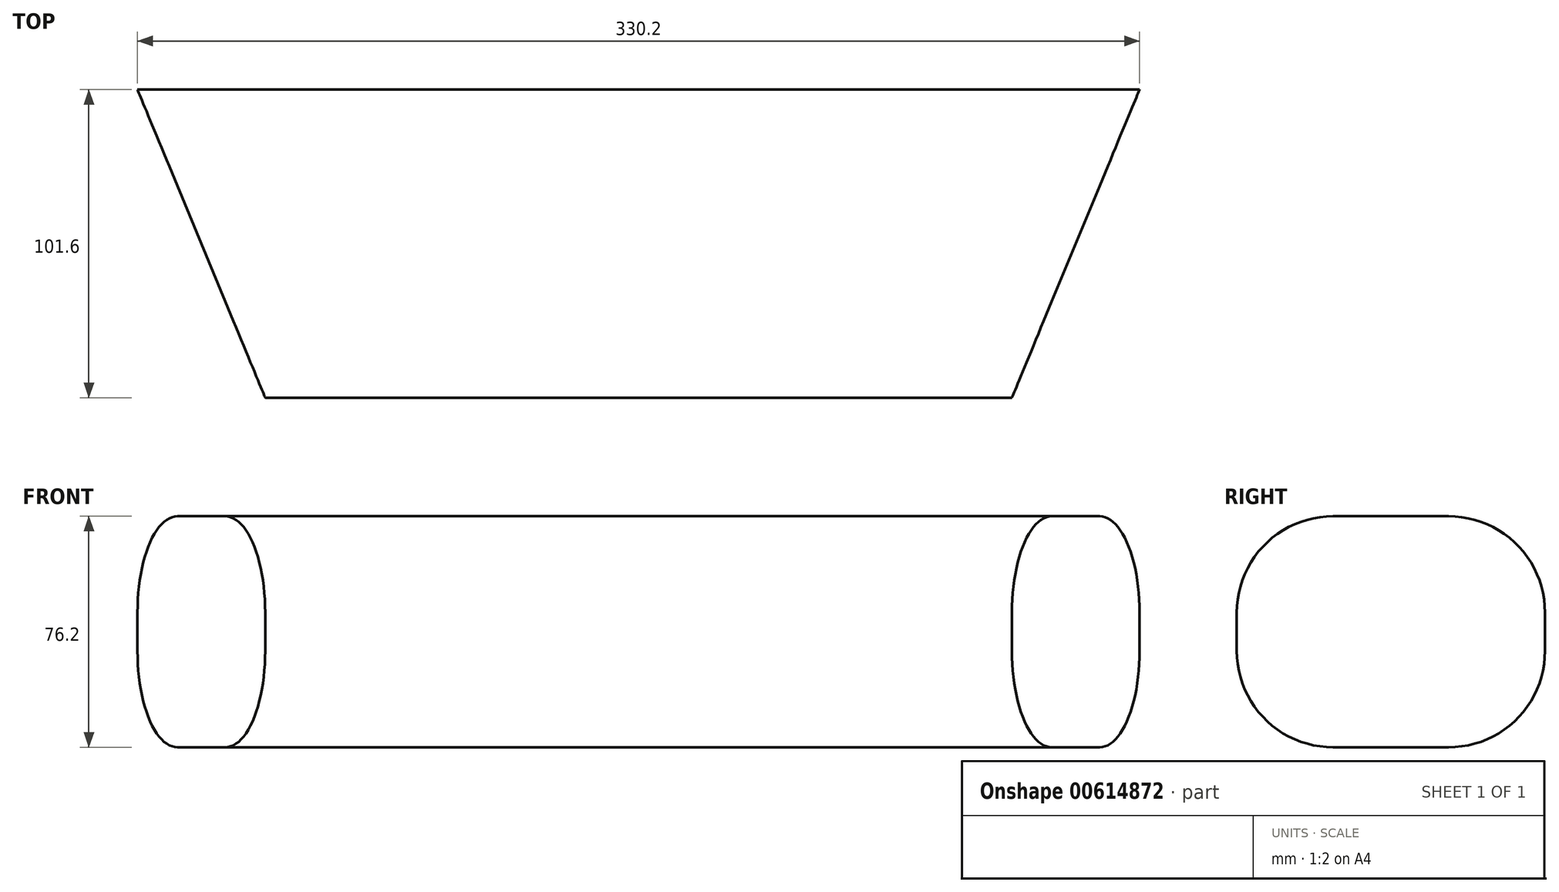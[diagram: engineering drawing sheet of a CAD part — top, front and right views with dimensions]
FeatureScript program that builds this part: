
annotation { "Feature Type Name" : "Feature", "Feature Type Description" : "" }
export const myFeature = defineFeature(function(context is Context, id is Id, definition is map)
    precondition{}
    {
        {
            var Q0;
            Q0=qCreatedBy(makeId("Top.planeOp"),FACE);
            var sketch = newSketch(context, id + "F0", { "sketchPlane" : qUnion([Q0])});
            skLineSegment(sketch, "E0", {"start": v(0, 0) * mm, "end": v(246.03, 0) * mm});
            skLineSegment(sketch, "E1", {"start": v(246.03, 0) * mm, "end": v(288.12, 101.6) * mm});
            skLineSegment(sketch, "E2", {"start": v(288.12, 101.6) * mm, "end": v(-42.08, 101.6) * mm});
            skLineSegment(sketch, "E3", {"start": v(-42.08, 101.6) * mm, "end": v(0, 0) * mm});
            skLineSegment(sketch, "E4.0", {"start": v(267.07, 50.8) * mm, "end": v(-21.04, 50.8) * mm});
            skSolve(sketch);
        }
        {
            var Q0;
            Q0 = qSketchRegion(id + "F0", true);
            extrude(context, id + "F1", {"entities" : qUnion([Q0]), "depth" : 76.2 * mm, "offsetDistance" : 25.4 * mm});
        }
        {
            var Q0;
            Q0=makeQuery(id+"F1.opExtrude","CAP_EDGE",EDGE,{"disambiguationData":[OSD([sQuery(id+"F0.wireOp",EDGE,"E2")])],"isStart":false});
            var Q1;
            Q1=makeQuery(id+"F1.opExtrude","CAP_EDGE",EDGE,{"disambiguationData":[OSD([sQuery(id+"F0.wireOp",EDGE,"E0")])],"isStart":false});
            var Q2;
            Q2=makeQuery(id+"F1.opExtrude","CAP_EDGE",EDGE,{"disambiguationData":[OSD([sQuery(id+"F0.wireOp",EDGE,"E0")])],"isStart":true});
            var Q3;
            Q3=makeQuery(id+"F1.opExtrude","CAP_EDGE",EDGE,{"disambiguationData":[OSD([sQuery(id+"F0.wireOp",EDGE,"E2")])],"isStart":true});
            fillet(context, id + "F2", {"entities" : qUnion([Q0, Q1, Q2, Q3]), "radius" : 31.75 * mm, "tangentPropagation" : true, "allowEdgeOverflow" : false});
        }
    });
